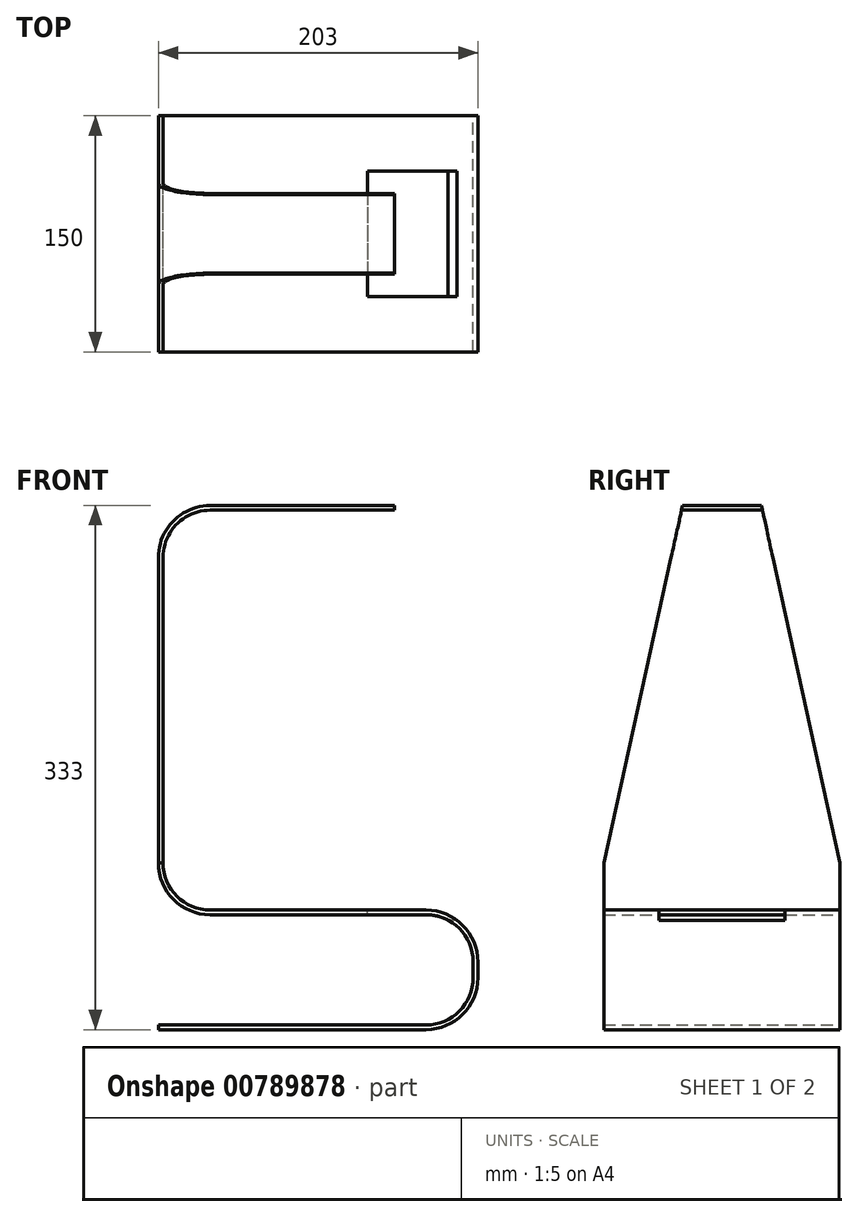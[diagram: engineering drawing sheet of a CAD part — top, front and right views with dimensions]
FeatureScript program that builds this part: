
annotation { "Feature Type Name" : "Feature", "Feature Type Description" : "" }
export const myFeature = defineFeature(function(context is Context, id is Id, definition is map)
    precondition{}
    {
        {
            var Q0;
            Q0=qCreatedBy(makeId("Front.planeOp"),FACE);
            var sketch = newSketch(context, id + "F0", { "sketchPlane" : qUnion([Q0])});
            skLineSegment(sketch, "E0.bottom", {"start": v(70, 35) * mm, "end": v(-67, 35) * mm});
            skLineSegment(sketch, "E0.top", {"start": v(70, -35) * mm, "end": v(-100, -35) * mm});
            skLineSegment(sketch, "E0.left", {"start": v(100, 5) * mm, "end": v(100, -5) * mm});
            skPoint(sketch, "E0.middle", {"position": v(0, 0) * mm});
            skLineSegment(sketch, "E1", {"start": v(-100, 68) * mm, "end": v(-100, 265) * mm});
            skLineSegment(sketch, "E2", {"start": v(-70, 295) * mm, "end": v(50, 295) * mm});
            skPoint(sketch, "E3.visualSharp", {"position": v(-100, 35) * mm});
            skArc(sketch, "E3.filletArc", {"start": v(-100, 68) * mm, "mid": v(-90.33, 44.67) * mm, "end": v(-67, 35) * mm});
            skPoint(sketch, "E4.visualSharp", {"position": v(-100, 295) * mm});
            skPoint(sketch, "E5.visualSharp", {"position": v(100, 35) * mm});
            skArc(sketch, "E5.filletArc", {"start": v(100, 5) * mm, "mid": v(91.21, 26.21) * mm, "end": v(70, 35) * mm});
            skPoint(sketch, "E6.visualSharp", {"position": v(100, -35) * mm});
            skArc(sketch, "E6.filletArc", {"start": v(70, -35) * mm, "mid": v(91.21, -26.21) * mm, "end": v(100, -5) * mm});
            skLineSegment(sketch, "E7.0", {"start": v(-70, 292) * mm, "end": v(50, 292) * mm});
            skLineSegment(sketch, "E7.2", {"start": v(-97, 68) * mm, "end": v(-97, 265) * mm});
            skArc(sketch, "E7.3", {"start": v(-97, 68) * mm, "mid": v(-88.21, 46.79) * mm, "end": v(-67, 38) * mm});
            skLineSegment(sketch, "E7.4", {"start": v(70, 38) * mm, "end": v(-67, 38) * mm});
            skLineSegment(sketch, "E7.5", {"start": v(70, -38) * mm, "end": v(-100, -38) * mm});
            skArc(sketch, "E7.6", {"start": v(70, -38) * mm, "mid": v(93.33, -28.33) * mm, "end": v(103, -5) * mm});
            skLineSegment(sketch, "E7.7", {"start": v(103, 5) * mm, "end": v(103, -5) * mm});
            skArc(sketch, "E7.8", {"start": v(103, 5) * mm, "mid": v(93.33, 28.33) * mm, "end": v(70, 38) * mm});
            skLineSegment(sketch, "E8", {"start": v(50, 295) * mm, "end": v(50, 292) * mm});
            skLineSegment(sketch, "E9", {"start": v(-100, -38) * mm, "end": v(-100, -35) * mm});
            skLineSegment(sketch, "E10", {"start": v(-97, 262) * mm, "end": v(-97, 265) * mm});
            skLineSegment(sketch, "E11", {"start": v(-100, 262) * mm, "end": v(-100, 265) * mm});
            skLineSegment(sketch, "E12", {"start": v(-67, 292) * mm, "end": v(-70, 292) * mm});
            skLineSegment(sketch, "E13", {"start": v(-67, 295) * mm, "end": v(-70, 295) * mm});
            skPoint(sketch, "E14.visualSharp", {"position": v(-97, 292) * mm});
            skArc(sketch, "E14.filletArc", {"start": v(-67, 292) * mm, "mid": v(-88.21, 283.21) * mm, "end": v(-97, 262) * mm});
            skArc(sketch, "E15.filletArc", {"start": v(-67, 295) * mm, "mid": v(-90.33, 285.33) * mm, "end": v(-100, 262) * mm});
            skSolve(sketch);
        }
        {
            var Q0;
            Q0=makeQuery(id+"F0.imprint","IMPRINT",FACE,{"disambiguationData":[TD([[makeQuery(id+"F0.imprint","IMPRINT",EDGE,{"derivedFrom":sQuery(id+"F0.wireOp",EDGE,"E0.bottom")}),-1.0]])]});
            var Q1;
            Q1=makeQuery(id+"F0.imprint","IMPRINT",FACE,{"disambiguationData":[TD([[makeQuery(id+"F0.imprint","IMPRINT",EDGE,{"derivedFrom":sQuery(id+"F0.wireOp",EDGE,"E0.bottom")}),-1.0]])]});
            var Q2;
            {var subQ0=sQuery(id+"F0.wireOp",EDGE,"E13");var subQ1=sQuery(id+"F0.wireOp",EDGE,"E10");var subQ2=makeQuery(id+"F0.imprint","INTERSECT",VERTEX,{"derivedFrom":[subQ1,subQ0]});Q2=makeQuery(id+"F0.imprint","IMPRINT",FACE,{"disambiguationData":[TD([[makeQuery(id+"F0.imprint","IMPRINT",EDGE,{"disambiguationData":[TD([[subQ2,1.0]])],"derivedFrom":subQ1}),1.0]])]});}
            extrude(context, id + "F1", {"entities" : qUnion([Q0, Q1, Q2]), "endBound" : BoundingType.SYMMETRIC, "depth" : 150 * mm});
        }
        {
            var Q0;
            Q0=makeQuery(id+"F1.opExtrude","SWEPT_FACE",FACE,{"disambiguationData":[OSD([sQuery(id+"F0.wireOp",EDGE,"E1")])]});
            var sketch = newSketch(context, id + "F2", { "sketchPlane" : qUnion([Q0])});
            skLineSegment(sketch, "E16", {"start": v(-75, 262) * mm, "end": v(-75, 295) * mm});
            skLineSegment(sketch, "E17", {"start": v(75, 262) * mm, "end": v(75, 295) * mm});
            skLineSegment(sketch, "E18", {"start": v(-75, 295) * mm, "end": v(-25, 295) * mm});
            skLineSegment(sketch, "E19", {"start": v(-25, 295) * mm, "end": v(25, 295) * mm});
            skLineSegment(sketch, "E20", {"start": v(25, 295) * mm, "end": v(75, 295) * mm});
            skLineSegment(sketch, "E21", {"start": v(-25, 295) * mm, "end": v(-75, 68) * mm});
            skLineSegment(sketch, "E22", {"start": v(25, 295) * mm, "end": v(75, 68) * mm});
            skSolve(sketch);
        }
        {
            var Q0;
            Q0=qSketchRegion(id+"F2",true);
            var Q1;
            {var subQ1=sQuery(id+"F0.wireOp",EDGE,"E1");var subQ2=makeQuery(id+"F1.opExtrude","CAP_EDGE",EDGE,{"disambiguationData":[OSD([subQ1])],"isStart":true});Q1=makeQuery(id+"F2.imprint","IMPRINT",FACE,{"disambiguationData":[TD([[makeQuery(id+"F2.imprint","IMPRINT",EDGE,{"derivedFrom":subQ2}),-1.0]])]});}
            var Q2;
            {var subQ0=sQuery(id+"F2.wireOp",EDGE,"E16");Q2=makeQuery(id+"F2.imprint","IMPRINT",FACE,{"disambiguationData":[TD([[makeQuery(id+"F2.imprint","IMPRINT",EDGE,{"derivedFrom":subQ0}),-1.0]])]});}
            var Q3;
            {var subQ0=sQuery(id+"F2.wireOp",EDGE,"E17");Q3=makeQuery(id+"F2.imprint","IMPRINT",FACE,{"disambiguationData":[TD([[makeQuery(id+"F2.imprint","IMPRINT",EDGE,{"derivedFrom":subQ0}),1.0]])]});}
            var Q4;
            {var subQ1=sQuery(id+"F0.wireOp",EDGE,"E1");var subQ2=makeQuery(id+"F1.opExtrude","CAP_EDGE",EDGE,{"disambiguationData":[OSD([subQ1])],"isStart":false});Q4=makeQuery(id+"F2.imprint","IMPRINT",FACE,{"disambiguationData":[TD([[makeQuery(id+"F2.imprint","IMPRINT",EDGE,{"derivedFrom":subQ2}),1.0]])]});}
            extrude(context, id + "F3", {"entities" : qUnion([Q0, Q1, Q2, Q3, Q4]), "operationType" : NewBodyOperationType.REMOVE, "oppositeDirection" : true, "depth" : 200 * mm});
        }
        {
            var Q0;
            Q0=makeQuery(id+"F1.opExtrude","SWEPT_FACE",FACE,{"disambiguationData":[OSD([sQuery(id+"F0.wireOp",EDGE,"E7.4")])]});
            var sketch = newSketch(context, id + "F4", { "sketchPlane" : qUnion([Q0])});
            skLineSegment(sketch, "E23", {"start": v(0, 0) * mm, "end": v(30, 0) * mm});
            skLineSegment(sketch, "E24", {"start": v(30, 0) * mm, "end": v(103, 0) * mm});
            skLineSegment(sketch, "E25", {"start": v(103, 0) * mm, "end": v(103, 40) * mm});
            skLineSegment(sketch, "E26", {"start": v(103, 0) * mm, "end": v(103, -40) * mm});
            skLineSegment(sketch, "E27", {"start": v(103, -40) * mm, "end": v(33, -40) * mm});
            skLineSegment(sketch, "E28", {"start": v(33, -40) * mm, "end": v(33, 40) * mm});
            skLineSegment(sketch, "E29", {"start": v(33, 40) * mm, "end": v(103, 40) * mm});
            skSolve(sketch);
        }
        {
            var Q0;
            {var subQ0=sQuery(id+"F4.wireOp",EDGE,"E28");var subQ5=sQuery(id+"F4.wireOp",EDGE,"E27");var subQ6=makeQuery(id+"F4.imprint","INTERSECT",VERTEX,{"derivedFrom":[subQ5,subQ0]});Q0=makeQuery(id+"F4.imprint","IMPRINT",FACE,{"disambiguationData":[TD([[makeQuery(id+"F4.imprint","IMPRINT",EDGE,{"disambiguationData":[TD([[subQ6,-1.0]])],"derivedFrom":subQ0}),-1.0]])]});}
            var Q1;
            {var subQ0=sQuery(id+"F4.wireOp",EDGE,"E26");Q1=makeQuery(id+"F4.imprint","IMPRINT",FACE,{"disambiguationData":[TD([[makeQuery(id+"F4.imprint","IMPRINT",EDGE,{"derivedFrom":subQ0}),-1.0]])]});}
            var Q2;
            {var subQ0=sQuery(id+"F4.wireOp",EDGE,"E25");Q2=makeQuery(id+"F4.imprint","IMPRINT",FACE,{"disambiguationData":[TD([[makeQuery(id+"F4.imprint","IMPRINT",EDGE,{"derivedFrom":subQ0}),1.0]])]});}
            var Q3;
            {var subQ0=sQuery(id+"F4.wireOp",EDGE,"E28");var subQ5=sQuery(id+"F4.wireOp",EDGE,"E29");var subQ6=makeQuery(id+"F4.imprint","INTERSECT",VERTEX,{"derivedFrom":[subQ0,subQ5]});Q3=makeQuery(id+"F4.imprint","IMPRINT",FACE,{"disambiguationData":[TD([[makeQuery(id+"F4.imprint","IMPRINT",EDGE,{"disambiguationData":[TD([[subQ6,1.0]])],"derivedFrom":subQ0}),-1.0]])]});}
            extrude(context, id + "F5", {"entities" : qUnion([Q0, Q1, Q2, Q3]), "operationType" : NewBodyOperationType.REMOVE, "endBound" : BoundingType.SYMMETRIC, "oppositeDirection" : true, "depth" : 13 * mm, "offsetDistance" : 25 * mm});
        }
    });
